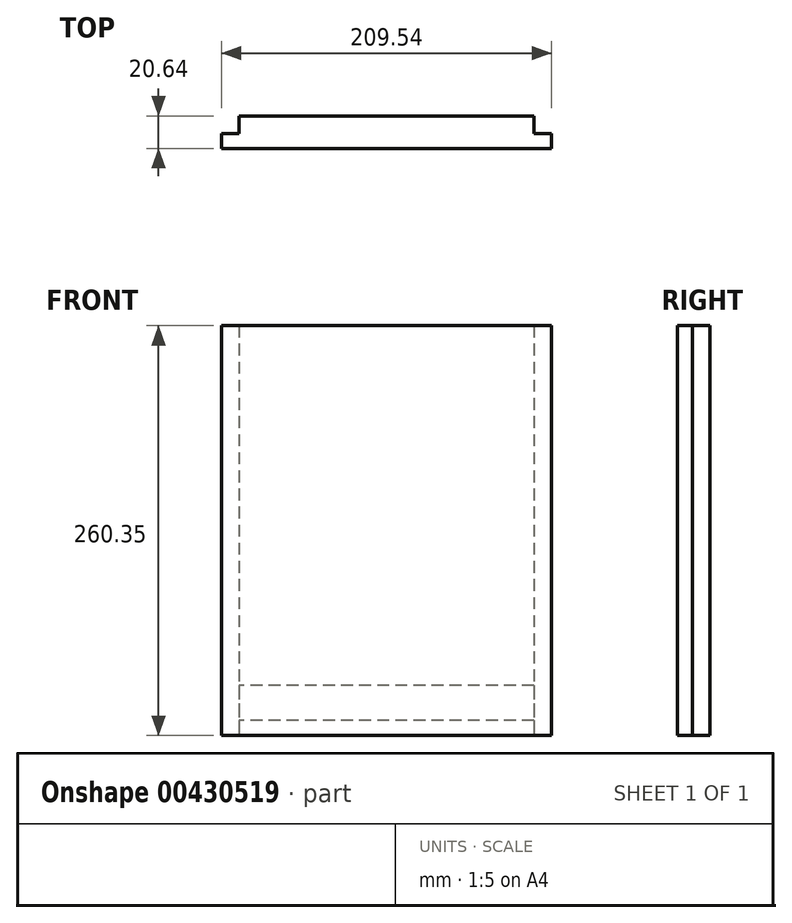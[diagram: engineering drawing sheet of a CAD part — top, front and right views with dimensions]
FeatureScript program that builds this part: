
annotation { "Feature Type Name" : "Feature", "Feature Type Description" : "" }
export const myFeature = defineFeature(function(context is Context, id is Id, definition is map)
    precondition{}
    {
        {
            var Q0;
            Q0=qCreatedBy(makeId("Top.planeOp"),FACE);
            var sketch = newSketch(context, id + "F0", { "sketchPlane" : qUnion([Q0])});
            skLineSegment(sketch, "E0", {"start": v(-104.78, 0) * mm, "end": v(104.78, 0) * mm});
            skLineSegment(sketch, "E1", {"start": v(104.78, 0) * mm, "end": v(104.77, 20.64) * mm});
            skLineSegment(sketch, "E2", {"start": v(104.77, 20.64) * mm, "end": v(-104.78, 20.64) * mm});
            skLineSegment(sketch, "E3", {"start": v(-104.78, 20.64) * mm, "end": v(-104.78, 0) * mm});
            skSolve(sketch);
        }
        {
            var Q0;
            Q0=makeQuery(id+"F0.imprint","IMPRINT",FACE,{"disambiguationData":[TD([[makeQuery(id+"F0.imprint","IMPRINT",EDGE,{"derivedFrom":sQuery(id+"F0.wireOp",EDGE,"E0")}),1.0]])]});
            extrude(context, id + "F1", {"entities" : qUnion([Q0]), "oppositeDirection" : true, "depth" : 260.35 * mm});
        }
        {
            var Q0;
            Q0=makeQuery(id+"F1.opExtrude","SWEPT_FACE",FACE,{"disambiguationData":[OSD([sQuery(id+"F0.wireOp",EDGE,"E2")])]});
            var sketch = newSketch(context, id + "F2", { "sketchPlane" : qUnion([Q0])});
            skLineSegment(sketch, "E4.bottom", {"start": v(-104.77, -228.6) * mm, "end": v(104.78, -228.6) * mm});
            skLineSegment(sketch, "E4.top", {"start": v(-104.78, -250.83) * mm, "end": v(104.78, -250.83) * mm});
            skLineSegment(sketch, "E4.left", {"start": v(-104.77, -228.6) * mm, "end": v(-104.77, -250.83) * mm});
            skLineSegment(sketch, "E4.right", {"start": v(104.78, -228.6) * mm, "end": v(104.78, -250.83) * mm});
            skSolve(sketch);
        }
        {
            var Q0;
            Q0=makeQuery(id+"F2.imprint","IMPRINT",FACE,{"disambiguationData":[TD([[makeQuery(id+"F2.imprint","IMPRINT",EDGE,{"derivedFrom":sQuery(id+"F2.wireOp",EDGE,"E4.bottom")}),-1.0]])]});
            extrude(context, id + "F3", {"entities" : qUnion([Q0]), "operationType" : NewBodyOperationType.REMOVE, "oppositeDirection" : true, "depth" : 7 / 406.4 * mm, "offsetDistance" : 25.4 * mm});
        }
        {
            var Q0;
            Q0=makeQuery(id+"F1.opExtrude","CAP_FACE",FACE,{"disambiguationData":[OSD([sQuery(id+"F0.wireOp",EDGE,"E0"),sQuery(id+"F0.wireOp",EDGE,"E1"),sQuery(id+"F0.wireOp",EDGE,"E2"),sQuery(id+"F0.wireOp",EDGE,"E3")])],"isStart":false});
            var sketch = newSketch(context, id + "F4", { "sketchPlane" : qUnion([Q0])});
            skLineSegment(sketch, "E5.bottom", {"start": v(-104.78, -20.64) * mm, "end": v(-93.66, -20.64) * mm});
            skLineSegment(sketch, "E5.top", {"start": v(-104.78, -9.53) * mm, "end": v(-93.66, -9.53) * mm});
            skLineSegment(sketch, "E5.left", {"start": v(-104.78, -20.64) * mm, "end": v(-104.78, -9.53) * mm});
            skLineSegment(sketch, "E5.right", {"start": v(-93.66, -20.64) * mm, "end": v(-93.66, -9.53) * mm});
            skLineSegment(sketch, "E6.bottom", {"start": v(104.77, -20.64) * mm, "end": v(93.66, -20.64) * mm});
            skLineSegment(sketch, "E6.top", {"start": v(104.77, -9.53) * mm, "end": v(93.66, -9.53) * mm});
            skLineSegment(sketch, "E6.left", {"start": v(104.77, -20.64) * mm, "end": v(104.77, -9.53) * mm});
            skLineSegment(sketch, "E6.right", {"start": v(93.66, -20.64) * mm, "end": v(93.66, -9.53) * mm});
            skSolve(sketch);
        }
        {
            var Q0;
            Q0=makeQuery(id+"F4.imprint","IMPRINT",FACE,{"disambiguationData":[TD([[makeQuery(id+"F4.imprint","IMPRINT",EDGE,{"derivedFrom":sQuery(id+"F4.wireOp",EDGE,"E5.bottom")}),-1.0]])]});
            var Q1;
            Q1=makeQuery(id+"F4.imprint","IMPRINT",FACE,{"disambiguationData":[TD([[makeQuery(id+"F4.imprint","IMPRINT",EDGE,{"derivedFrom":sQuery(id+"F4.wireOp",EDGE,"E6.bottom")}),-1.0]])]});
            extrude(context, id + "F5", {"entities" : qUnion([Q0, Q1]), "operationType" : NewBodyOperationType.REMOVE, "endBound" : BoundingType.THROUGH_ALL, "oppositeDirection" : true, "depth" : 25.4 * mm, "offsetDistance" : 25.4 * mm});
        }
    });
